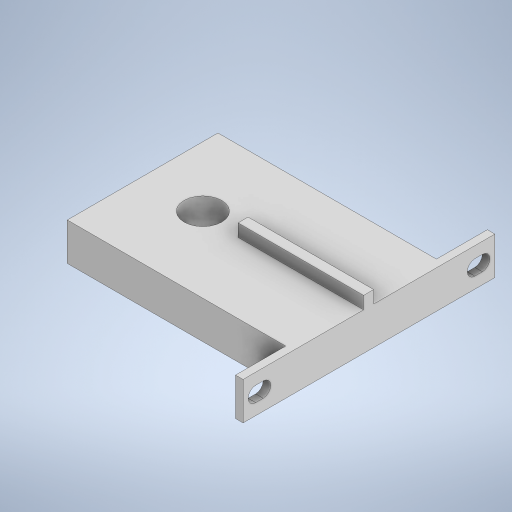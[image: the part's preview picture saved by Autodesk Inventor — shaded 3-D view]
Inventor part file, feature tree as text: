
AUTODESK INVENTOR PART (.ipt)
format: ipt  version: 2023 (Build 270158000, 158)  size: 295,936 bytes
history: native  units: mm
features: other x3, extrude x3, sketch x3
ambient origin geometry x8: Origin, YZ Plane, XZ Plane, XY Plane, X Axis, Y Axis, Z Axis, Center Point
bodies: Body1 (feature_tree)
feature tree (9):
  other  "Твердое тело1"
  extrude  "Выдавливание1"  Depth=90.0mm
  other  "РабПлоскость3"
  extrude  "Выдавливание3"  Depth=60.0mm
  other  "РабПлоскость1"
  sketch  "Эскиз6"
  extrude  "Выдавливание7"  Depth=15.0mm TaperAngle=0.0deg
  sketch  "Эскиз3"
  sketch  "Эскиз7"
